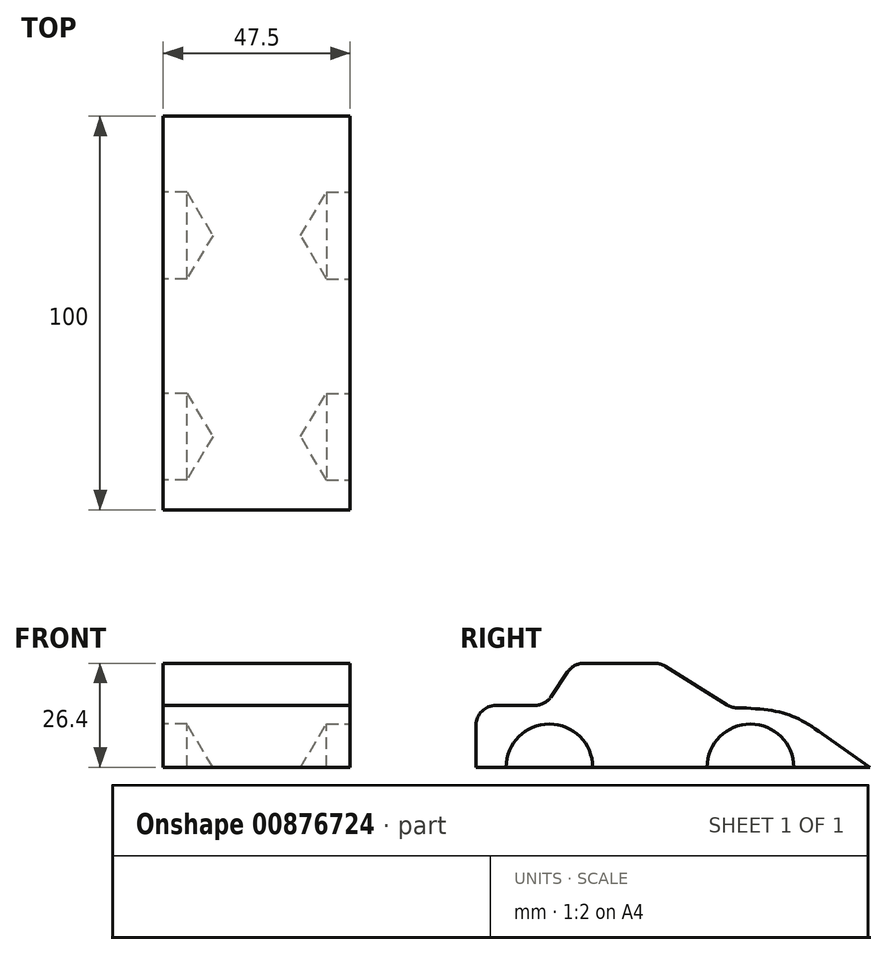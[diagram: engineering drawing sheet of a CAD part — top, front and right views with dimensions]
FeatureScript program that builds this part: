
annotation { "Feature Type Name" : "Feature", "Feature Type Description" : "" }
export const myFeature = defineFeature(function(context is Context, id is Id, definition is map)
    precondition{}
    {
        {
            var Q0;
            Q0=qCreatedBy(makeId("Right.planeOp"),FACE);
            var sketch = newSketch(context, id + "F0", { "sketchPlane" : qUnion([Q0])});
            skLineSegment(sketch, "E0.top", {"start": v(50, -20) * mm, "end": v(-50, -20) * mm});
            skLineSegment(sketch, "E0.right", {"start": v(-50, -4.3) * mm, "end": v(-50, -20) * mm});
            skPoint(sketch, "E0.middle", {"position": v(0, 0) * mm});
            skLineSegment(sketch, "E1", {"start": v(50, -20) * mm, "end": v(37.98, -11.48) * mm});
            skFitSpline(sketch, "E2", {"points": [v(37.98, -11.48) * mm, v(26.91, -5.95) * mm, v(7.18, -4.84) * mm], "startDerivative": vector(-28.8, 20.04) * mm, "endDerivative": vector(-43.6, 0) * mm});
            skPoint(sketch, "E0.bottom.end.orphan", {"position": v(-50, 20) * mm});
            skPoint(sketch, "E0.left.start.orphan", {"position": v(50, 20) * mm});
            skLineSegment(sketch, "E3", {"start": v(-50, -4.3) * mm, "end": v(-32.46, -4.3) * mm});
            skLineSegment(sketch, "E4", {"start": v(-32.46, -4.3) * mm, "end": v(-25.28, 6.4) * mm});
            skLineSegment(sketch, "E5", {"start": v(-25.28, 6.4) * mm, "end": v(-3.15, 6.4) * mm});
            skLineSegment(sketch, "E6", {"start": v(-3.15, 6.4) * mm, "end": v(14.89, -4.88) * mm});
            skSolve(sketch);
        }
        {
            var Q0;
            Q0=makeQuery(id+"F0.imprint","IMPRINT",FACE,{"disambiguationData":[TD([[makeQuery(id+"F0.imprint","IMPRINT",EDGE,{"derivedFrom":sQuery(id+"F0.wireOp",EDGE,"E0.top")}),-1.0]])]});
            extrude(context, id + "F1", {"entities" : qUnion([Q0]), "endBound" : BoundingType.SYMMETRIC, "depth" : 45 * mm, "offsetDistance" : 25 * mm});
        }
        {
            var Q0;
            Q0 = qSketchRegion(id + "F0", true);
            extrude(context, id + "F2", {"entities" : qUnion([Q0]), "operationType" : NewBodyOperationType.ADD, "depth" : 25 * mm, "offsetDistance" : 25 * mm});
        }
        {
            var Q0;
            {var subQ0=sQuery(id+"F0.wireOp",EDGE,"E5");var subQ1=sQuery(id+"F0.wireOp",EDGE,"E4");Q0=makeQuery(id+"F2.boolean.opBoolean","MERGE",EDGE,{"derivedFrom":[makeQuery(id+"F1.opExtrude","SWEPT_EDGE",EDGE,{"disambiguationData":[OSD([subQ1,subQ0])]}),makeQuery(id+"F2.opExtrude","SWEPT_EDGE",EDGE,{"disambiguationData":[OSD([subQ1,subQ0])]})]});}
            var Q1;
            {var subQ0=sQuery(id+"F0.wireOp",EDGE,"E4");var subQ1=sQuery(id+"F0.wireOp",EDGE,"E3");Q1=makeQuery(id+"F2.boolean.opBoolean","MERGE",EDGE,{"derivedFrom":[makeQuery(id+"F1.opExtrude","SWEPT_EDGE",EDGE,{"disambiguationData":[OSD([subQ1,subQ0])]}),makeQuery(id+"F2.opExtrude","SWEPT_EDGE",EDGE,{"disambiguationData":[OSD([subQ1,subQ0])]})]});}
            var Q2;
            {var subQ0=sQuery(id+"F0.wireOp",EDGE,"E3");var subQ1=sQuery(id+"F0.wireOp",EDGE,"E0.right");Q2=makeQuery(id+"F2.boolean.opBoolean","MERGE",EDGE,{"derivedFrom":[makeQuery(id+"F1.opExtrude","SWEPT_EDGE",EDGE,{"disambiguationData":[OSD([subQ1,subQ0])]}),makeQuery(id+"F2.opExtrude","SWEPT_EDGE",EDGE,{"disambiguationData":[OSD([subQ1,subQ0])]})]});}
            var Q3;
            {var subQ0=sQuery(id+"F0.wireOp",EDGE,"E6");var subQ1=sQuery(id+"F0.wireOp",EDGE,"E5");Q3=makeQuery(id+"F2.boolean.opBoolean","MERGE",EDGE,{"derivedFrom":[makeQuery(id+"F1.opExtrude","SWEPT_EDGE",EDGE,{"disambiguationData":[OSD([subQ1,subQ0])]}),makeQuery(id+"F2.opExtrude","SWEPT_EDGE",EDGE,{"disambiguationData":[OSD([subQ1,subQ0])]})]});}
            var Q4;
            {var subQ0=sQuery(id+"F0.wireOp",EDGE,"E6");var subQ1=sQuery(id+"F0.wireOp",EDGE,"E2");Q4=makeQuery(id+"F2.boolean.opBoolean","MERGE",EDGE,{"derivedFrom":[makeQuery(id+"F1.opExtrude","SWEPT_EDGE",EDGE,{"disambiguationData":[OSD([subQ1,subQ0])]}),makeQuery(id+"F2.opExtrude","SWEPT_EDGE",EDGE,{"disambiguationData":[OSD([subQ1,subQ0])]})]});}
            fillet(context, id + "F3", {"entities" : qUnion([Q0, Q1, Q2, Q3, Q4]), "radius" : 5 * mm, "tangentPropagation" : true, "allowEdgeOverflow" : false});
        }
        {
            var Q0;
            Q0=makeQuery(id+"F2.opExtrude","CAP_FACE",FACE,{"disambiguationData":[OSD([sQuery(id+"F0.wireOp",EDGE,"E0.top"),sQuery(id+"F0.wireOp",EDGE,"E0.right"),sQuery(id+"F0.wireOp",EDGE,"E1"),sQuery(id+"F0.wireOp",EDGE,"E2"),sQuery(id+"F0.wireOp",EDGE,"E3"),sQuery(id+"F0.wireOp",EDGE,"E4"),sQuery(id+"F0.wireOp",EDGE,"E5"),sQuery(id+"F0.wireOp",EDGE,"E6")])],"isStart":false});
            var sketch = newSketch(context, id + "F4", { "sketchPlane" : qUnion([Q0])});
            skCircle(sketch, "E7", {"center": v(19.7, -20) * mm, "radius": 11 * mm});
            skCircle(sketch, "E8", {"center": v(-31.4, -20) * mm, "radius": 11 * mm});
            skSolve(sketch);
        }
        {
            var Q0;
            Q0=sQuery(id+"F4.wireOp",VERTEX,"E8.center");
            var Q1;
            Q1=makeQuery(id+"F1.opExtrude","SWEPT_BODY",BODY,{"disambiguationData":[OSD([sQuery(id+"F0.wireOp",EDGE,"E0.top"),sQuery(id+"F0.wireOp",EDGE,"E0.right"),sQuery(id+"F0.wireOp",EDGE,"E1"),sQuery(id+"F0.wireOp",EDGE,"E2"),sQuery(id+"F0.wireOp",EDGE,"E3"),sQuery(id+"F0.wireOp",EDGE,"E4"),sQuery(id+"F0.wireOp",EDGE,"E5"),sQuery(id+"F0.wireOp",EDGE,"E6")])]});
            hole(context, id + "F5", {"style" : HoleStyle.SIMPLE, "endStyle" : HoleEndStyle.BLIND, "holeDiameter" : 22 * mm, "majorDiameter" : 5 * mm, "holeDepth" : 6 * mm, "isTappedThrough" : true, "tappedDepth" : 12 * mm, "tapClearance" : 3, "startFromSketch" : true, "locations" : qUnion([Q0]), "scope" : qUnion([Q1])});
        }
        {
            var Q0;
            Q0=sQuery(id+"F4.wireOp",VERTEX,"E7.center");
            var Q1;
            Q1=makeQuery(id+"F1.opExtrude","SWEPT_BODY",BODY,{"disambiguationData":[OSD([sQuery(id+"F0.wireOp",EDGE,"E0.top"),sQuery(id+"F0.wireOp",EDGE,"E0.right"),sQuery(id+"F0.wireOp",EDGE,"E1"),sQuery(id+"F0.wireOp",EDGE,"E2"),sQuery(id+"F0.wireOp",EDGE,"E3"),sQuery(id+"F0.wireOp",EDGE,"E4"),sQuery(id+"F0.wireOp",EDGE,"E5"),sQuery(id+"F0.wireOp",EDGE,"E6")])]});
            hole(context, id + "F6", {"style" : HoleStyle.SIMPLE, "endStyle" : HoleEndStyle.BLIND, "holeDiameter" : 22 * mm, "majorDiameter" : 5 * mm, "holeDepth" : 6 * mm, "isTappedThrough" : true, "tappedDepth" : 12 * mm, "tapClearance" : 3, "startFromSketch" : true, "locations" : qUnion([Q0]), "scope" : qUnion([Q1])});
        }
        {
            var Q0;
            Q0=makeQuery(id+"F1.opExtrude","CAP_FACE",FACE,{"disambiguationData":[OSD([sQuery(id+"F0.wireOp",EDGE,"E0.top"),sQuery(id+"F0.wireOp",EDGE,"E0.right"),sQuery(id+"F0.wireOp",EDGE,"E1"),sQuery(id+"F0.wireOp",EDGE,"E2"),sQuery(id+"F0.wireOp",EDGE,"E3"),sQuery(id+"F0.wireOp",EDGE,"E4"),sQuery(id+"F0.wireOp",EDGE,"E5"),sQuery(id+"F0.wireOp",EDGE,"E6")])],"isStart":true});
            var sketch = newSketch(context, id + "F7", { "sketchPlane" : qUnion([Q0])});
            skCircle(sketch, "E9", {"center": v(-19.7, -20) * mm, "radius": 11 * mm});
            skCircle(sketch, "E10", {"center": v(31.42, -20) * mm, "radius": 11 * mm});
            skSolve(sketch);
        }
        {
            var Q0;
            Q0=sQuery(id+"F7.wireOp",VERTEX,"E9.center");
            var Q1;
            Q1=makeQuery(id+"F1.opExtrude","SWEPT_BODY",BODY,{"disambiguationData":[OSD([sQuery(id+"F0.wireOp",EDGE,"E0.top"),sQuery(id+"F0.wireOp",EDGE,"E0.right"),sQuery(id+"F0.wireOp",EDGE,"E1"),sQuery(id+"F0.wireOp",EDGE,"E2"),sQuery(id+"F0.wireOp",EDGE,"E3"),sQuery(id+"F0.wireOp",EDGE,"E4"),sQuery(id+"F0.wireOp",EDGE,"E5"),sQuery(id+"F0.wireOp",EDGE,"E6")])]});
            hole(context, id + "F8", {"style" : HoleStyle.SIMPLE, "endStyle" : HoleEndStyle.BLIND, "holeDiameter" : 22 * mm, "majorDiameter" : 5 * mm, "holeDepth" : 6 * mm, "isTappedThrough" : true, "tappedDepth" : 12 * mm, "tapClearance" : 3, "startFromSketch" : true, "locations" : qUnion([Q0]), "scope" : qUnion([Q1])});
        }
        {
            var Q0;
            Q0=sQuery(id+"F7.wireOp",VERTEX,"E10.center");
            var Q1;
            Q1=makeQuery(id+"F1.opExtrude","SWEPT_BODY",BODY,{"disambiguationData":[OSD([sQuery(id+"F0.wireOp",EDGE,"E0.top"),sQuery(id+"F0.wireOp",EDGE,"E0.right"),sQuery(id+"F0.wireOp",EDGE,"E1"),sQuery(id+"F0.wireOp",EDGE,"E2"),sQuery(id+"F0.wireOp",EDGE,"E3"),sQuery(id+"F0.wireOp",EDGE,"E4"),sQuery(id+"F0.wireOp",EDGE,"E5"),sQuery(id+"F0.wireOp",EDGE,"E6")])]});
            hole(context, id + "F9", {"style" : HoleStyle.SIMPLE, "endStyle" : HoleEndStyle.BLIND, "holeDiameter" : 22 * mm, "majorDiameter" : 5 * mm, "holeDepth" : 6 * mm, "isTappedThrough" : true, "tappedDepth" : 12 * mm, "tapClearance" : 3, "startFromSketch" : true, "locations" : qUnion([Q0]), "scope" : qUnion([Q1])});
        }
    });
